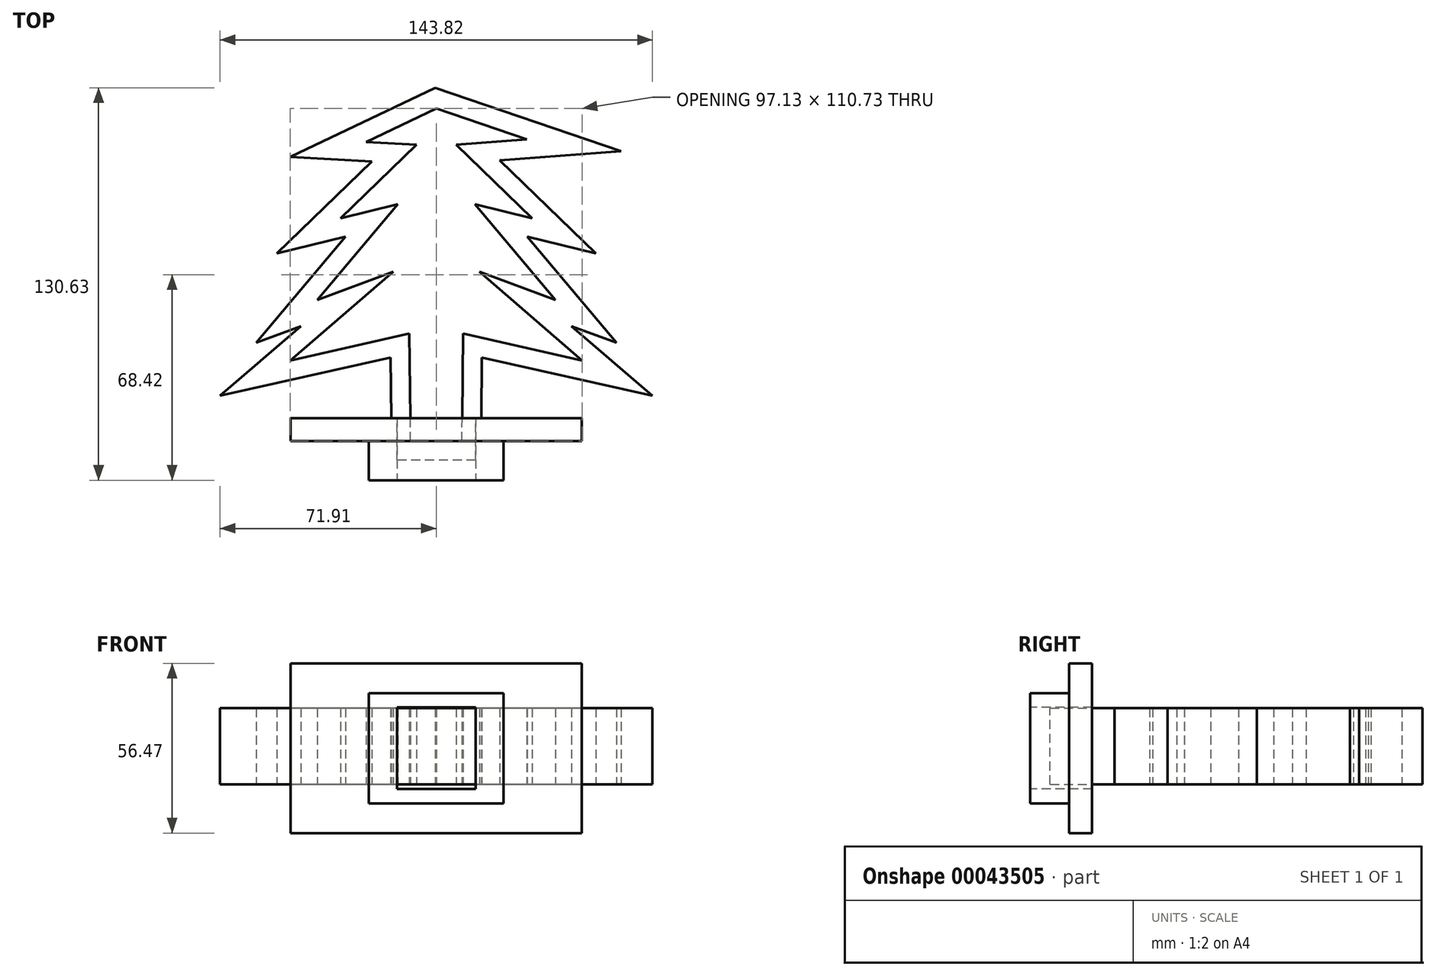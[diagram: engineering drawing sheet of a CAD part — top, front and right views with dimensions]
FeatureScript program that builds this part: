
annotation { "Feature Type Name" : "Feature", "Feature Type Description" : "" }
export const myFeature = defineFeature(function(context is Context, id is Id, definition is map)
    precondition{}
    {
        {
            var Q0;
            Q0=qCreatedBy(makeId("Top.planeOp"),FACE);
            var sketch = newSketch(context, id + "F0", { "sketchPlane" : qUnion([Q0])});
            skLineSegment(sketch, "E0", {"start": v(0, -35.74) * mm, "end": v(-8.55, -35.74) * mm});
            skLineSegment(sketch, "E1", {"start": v(-8.55, -35.74) * mm, "end": v(-8.94, 0) * mm});
            skLineSegment(sketch, "E2", {"start": v(-8.94, 0) * mm, "end": v(-48.57, -8.94) * mm});
            skLineSegment(sketch, "E3", {"start": v(-48.57, -8.94) * mm, "end": v(-14.38, 20.6) * mm});
            skLineSegment(sketch, "E4", {"start": v(-14.38, 20.6) * mm, "end": v(-39.63, 11.27) * mm});
            skLineSegment(sketch, "E5", {"start": v(-39.63, 11.27) * mm, "end": v(-12.82, 43.13) * mm});
            skLineSegment(sketch, "E6", {"start": v(-12.82, 43.13) * mm, "end": v(-31.86, 38.46) * mm});
            skLineSegment(sketch, "E7", {"start": v(-31.86, 38.46) * mm, "end": v(-6.6, 62.94) * mm});
            skLineSegment(sketch, "E8", {"start": v(-6.6, 62.94) * mm, "end": v(-23.38, 63.83) * mm});
            skLineSegment(sketch, "E9", {"start": v(-23.38, 63.83) * mm, "end": v(0, 74.98) * mm});
            skLineSegment(sketch, "E10.MirrorCS", {"start": v(8.55, -35.74) * mm, "end": v(8.94, 0) * mm});
            skLineSegment(sketch, "E11.MirrorCS", {"start": v(6.6, 62.94) * mm, "end": v(30.1, 64.7) * mm});
            skLineSegment(sketch, "E12.MirrorCS", {"start": v(14.38, 20.6) * mm, "end": v(39.63, 11.27) * mm});
            skLineSegment(sketch, "E13.MirrorCS", {"start": v(31.86, 38.46) * mm, "end": v(6.6, 62.94) * mm});
            skLineSegment(sketch, "E14.MirrorCS", {"start": v(39.63, 11.27) * mm, "end": v(12.82, 43.13) * mm});
            skLineSegment(sketch, "E15.MirrorCS", {"start": v(8.94, 0) * mm, "end": v(48.57, -8.94) * mm});
            skLineSegment(sketch, "E16.MirrorCS", {"start": v(12.82, 43.13) * mm, "end": v(31.86, 38.46) * mm});
            skLineSegment(sketch, "E17.MirrorCS", {"start": v(48.57, -8.94) * mm, "end": v(14.38, 20.6) * mm});
            skLineSegment(sketch, "E18.MirrorCS", {"start": v(30.1, 64.7) * mm, "end": v(0, 74.98) * mm});
            skLineSegment(sketch, "E19", {"start": v(8.55, -35.74) * mm, "end": v(0, -35.74) * mm});
            skLineSegment(sketch, "E20.0", {"start": v(-14.83, -42.1) * mm, "end": v(-15.2, -7.92) * mm});
            skLineSegment(sketch, "E20.1", {"start": v(0, -42.1) * mm, "end": v(-14.83, -42.1) * mm});
            skLineSegment(sketch, "E20.2", {"start": v(14.83, -42.1) * mm, "end": v(0, -42.1) * mm});
            skLineSegment(sketch, "E20.3", {"start": v(14.83, -42.1) * mm, "end": v(15.2, -7.92) * mm});
            skLineSegment(sketch, "E20.4", {"start": v(15.2, -7.92) * mm, "end": v(71.91, -20.71) * mm});
            skLineSegment(sketch, "E20.5", {"start": v(-15.2, -7.92) * mm, "end": v(-71.91, -20.71) * mm});
            skLineSegment(sketch, "E20.6", {"start": v(71.91, -20.71) * mm, "end": v(45.04, 2.5) * mm});
            skLineSegment(sketch, "E20.7", {"start": v(45.04, 2.5) * mm, "end": v(59.93, -3) * mm});
            skLineSegment(sketch, "E20.8", {"start": v(59.93, -3) * mm, "end": v(30.2, 32.33) * mm});
            skLineSegment(sketch, "E20.9", {"start": v(30.2, 32.33) * mm, "end": v(53.1, 26.73) * mm});
            skLineSegment(sketch, "E20.10", {"start": v(-30.2, 32.33) * mm, "end": v(-53.1, 26.73) * mm});
            skLineSegment(sketch, "E20.11", {"start": v(-59.93, -3) * mm, "end": v(-30.2, 32.33) * mm});
            skLineSegment(sketch, "E20.12", {"start": v(-45.04, 2.5) * mm, "end": v(-59.93, -3) * mm});
            skLineSegment(sketch, "E20.13", {"start": v(-71.91, -20.71) * mm, "end": v(-45.04, 2.5) * mm});
            skLineSegment(sketch, "E20.14", {"start": v(-53.1, 26.73) * mm, "end": v(-21.48, 57.37) * mm});
            skLineSegment(sketch, "E20.15", {"start": v(-21.48, 57.37) * mm, "end": v(-48.64, 58.81) * mm});
            skLineSegment(sketch, "E20.16", {"start": v(-48.64, 58.81) * mm, "end": v(-0.4, 81.83) * mm});
            skLineSegment(sketch, "E20.17", {"start": v(61.48, 60.7) * mm, "end": v(-0.4, 81.83) * mm});
            skLineSegment(sketch, "E20.18", {"start": v(21.17, 57.67) * mm, "end": v(61.48, 60.7) * mm});
            skLineSegment(sketch, "E20.19", {"start": v(53.1, 26.73) * mm, "end": v(21.17, 57.67) * mm});
            skSolve(sketch);
        }
        {
            var Q0;
            Q0 = qSketchRegion(id + "F0", true);
            extrude(context, id + "F1", {"entities" : qUnion([Q0]), "depth" : 25.4 * mm});
        }
        {
            var Q0;
            Q0=makeQuery(id+"F1.opExtrude","SWEPT_FACE",FACE,{"disambiguationData":[OSD([sQuery(id+"F0.wireOp",EDGE,"E0"),sQuery(id+"F0.wireOp",EDGE,"E19")])]});
            var sketch = newSketch(context, id + "F2", { "sketchPlane" : qUnion([Q0])});
            skLineSegment(sketch, "E21.rect.bottom", {"start": v(13.08, -1.55) * mm, "end": v(-13.08, -1.55) * mm});
            skLineSegment(sketch, "E21.rect.top", {"start": v(13.08, 25.59) * mm, "end": v(-13.08, 25.59) * mm});
            skLineSegment(sketch, "E21.rect.left", {"start": v(13.08, -1.55) * mm, "end": v(13.08, 25.59) * mm});
            skLineSegment(sketch, "E21.rect.right", {"start": v(-13.08, -1.55) * mm, "end": v(-13.08, 25.59) * mm});
            skPoint(sketch, "E21.rect.middle", {"position": v(0, 12.02) * mm});
            skLineSegment(sketch, "E22.rect.bottom", {"start": v(22.44, -6.32) * mm, "end": v(-22.44, -6.32) * mm});
            skLineSegment(sketch, "E22.rect.top", {"start": v(22.44, 30.35) * mm, "end": v(-22.44, 30.35) * mm});
            skLineSegment(sketch, "E22.rect.left", {"start": v(22.44, -6.32) * mm, "end": v(22.44, 30.35) * mm});
            skLineSegment(sketch, "E22.rect.right", {"start": v(-22.44, -6.32) * mm, "end": v(-22.44, 30.35) * mm});
            skLineSegment(sketch, "E23.rect.bottom", {"start": v(48.47, -16.22) * mm, "end": v(-48.47, -16.22) * mm});
            skLineSegment(sketch, "E23.rect.top", {"start": v(48.47, 40.25) * mm, "end": v(-48.47, 40.25) * mm});
            skLineSegment(sketch, "E23.rect.left", {"start": v(48.47, -16.22) * mm, "end": v(48.47, 40.25) * mm});
            skLineSegment(sketch, "E23.rect.right", {"start": v(-48.47, -16.22) * mm, "end": v(-48.47, 40.25) * mm});
            skSolve(sketch);
        }
        {
            var Q0;
            Q0 = qSketchRegion(id + "F2", true);
            var Q1;
            Q1=makeQuery(id+"F2.imprint","IMPRINT",FACE,{"disambiguationData":[TD([[makeQuery(id+"F2.imprint","IMPRINT",EDGE,{"derivedFrom":sQuery(id+"F2.wireOp",EDGE,"E21.rect.bottom")}),1.0]])]});
            extrude(context, id + "F3", {"entities" : qUnion([Q0, Q1]), "depth" : 7.62 * mm});
        }
        {
            var Q0;
            Q0=makeQuery(id+"F2.imprint","IMPRINT",FACE,{"disambiguationData":[TD([[makeQuery(id+"F2.imprint","IMPRINT",EDGE,{"derivedFrom":sQuery(id+"F2.wireOp",EDGE,"E21.rect.bottom")}),1.0]])]});
            extrude(context, id + "F4", {"entities" : qUnion([Q0]), "operationType" : NewBodyOperationType.ADD, "oppositeDirection" : true, "depth" : 13.06 * mm});
        }
    });
